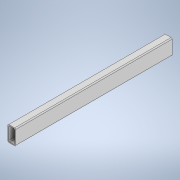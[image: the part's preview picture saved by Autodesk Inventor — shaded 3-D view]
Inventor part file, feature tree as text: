
AUTODESK INVENTOR PART (.ipt)
format: ipt  version: 2020 (Build 240168000, 168)  size: 121,856 bytes
history: native  units: in
note: dims shown in document units (in); Inventor stores cm internally (conversion verified against a paired STEP export)
features: extrude x1, sketch x1
ambient origin geometry x8: Origin, YZ Plane, XZ Plane, XY Plane, X Axis, Y Axis, Z Axis, Center Point
bodies: Solid1 (feature_tree)
feature tree (2):
  extrude  "Extrusion1"  Depth=1.0in
  sketch  "Sketch1"  dims[d0=2.0in d1=1.0in d2=0.125in d3=0.125in d4=0.125in d5=0.125in d6=0.125in d7=0.125in d8=0.125in d9=0.125in d10=0.125in d11=20.0in d12=0.0in]
